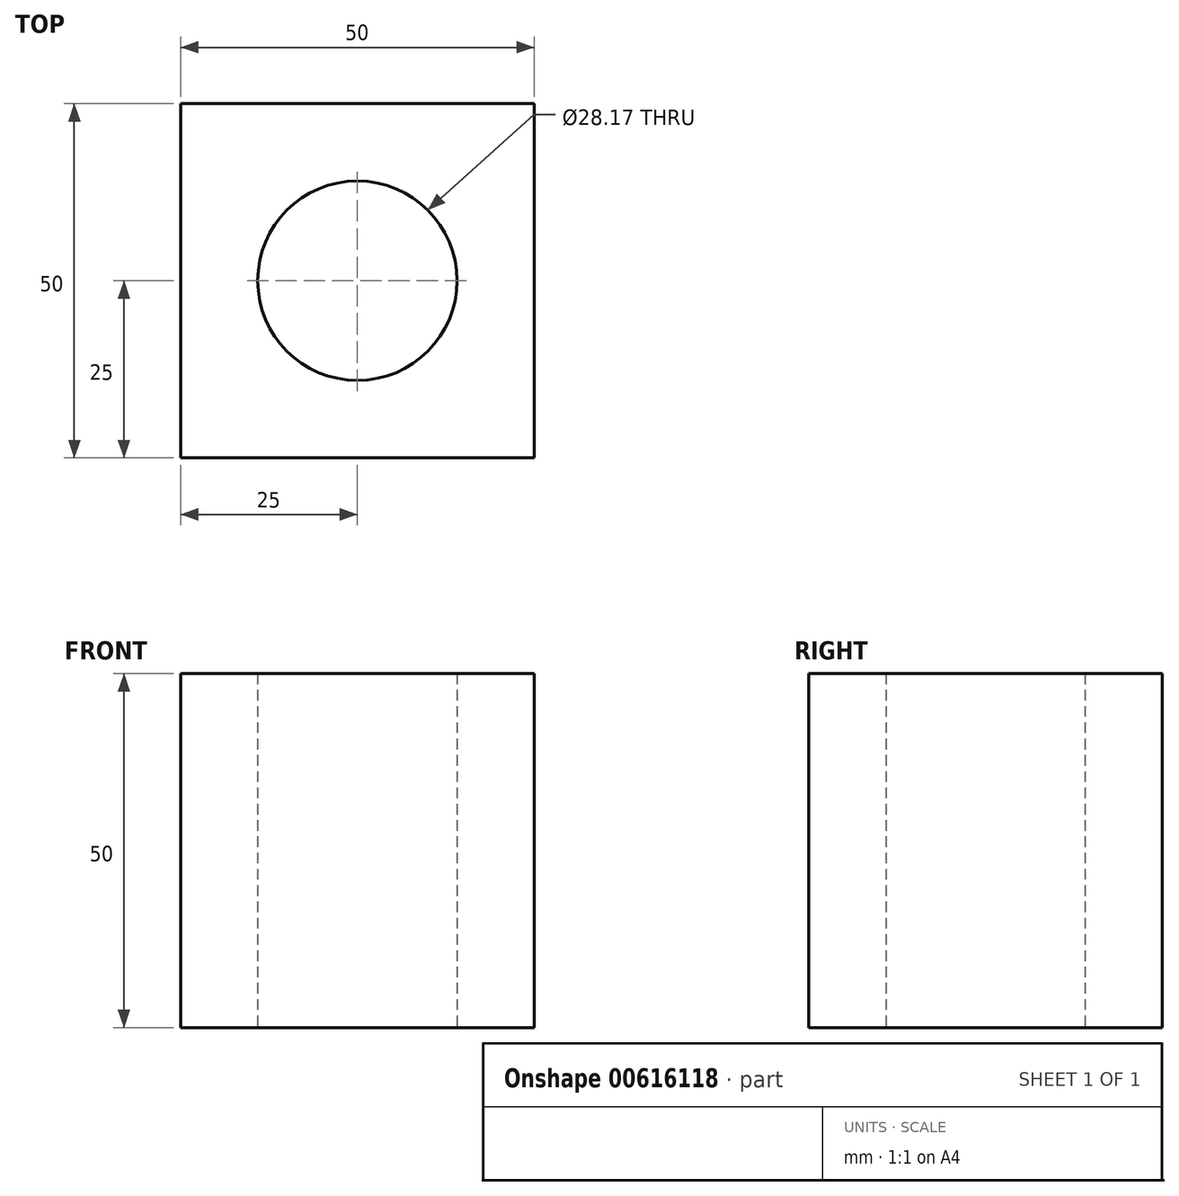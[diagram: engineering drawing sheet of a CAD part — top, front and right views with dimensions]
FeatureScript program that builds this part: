
annotation { "Feature Type Name" : "Feature", "Feature Type Description" : "" }
export const myFeature = defineFeature(function(context is Context, id is Id, definition is map)
    precondition{}
    {
        {
            var Q0;
            Q0=qCreatedBy(makeId("Top.planeOp"),FACE);
            var sketch = newSketch(context, id + "F0", { "sketchPlane" : qUnion([Q0])});
            skLineSegment(sketch, "E0.bottom", {"start": v(25, 25) * mm, "end": v(-25, 25) * mm});
            skLineSegment(sketch, "E0.top", {"start": v(25, -25) * mm, "end": v(-25, -25) * mm});
            skLineSegment(sketch, "E0.left", {"start": v(25, 25) * mm, "end": v(25, -25) * mm});
            skLineSegment(sketch, "E0.right", {"start": v(-25, 25) * mm, "end": v(-25, -25) * mm});
            skPoint(sketch, "E0.middle", {"position": v(0, 0) * mm});
            skSolve(sketch);
        }
        {
            var Q0;
            Q0=makeQuery(id+"F0.imprint","IMPRINT",FACE,{"disambiguationData":[TD([[makeQuery(id+"F0.imprint","IMPRINT",EDGE,{"derivedFrom":sQuery(id+"F0.wireOp",EDGE,"E0.bottom")}),1.0]])]});
            extrude(context, id + "F1", {"entities" : qUnion([Q0]), "depth" : 50 * mm, "offsetDistance" : 25 * mm});
        }
        {
            var Q0;
            Q0=qCreatedBy(makeId("Top.planeOp"),FACE);
            var sketch = newSketch(context, id + "F2", { "sketchPlane" : qUnion([Q0])});
            skCircle(sketch, "E1", {"center": v(0, 0) * mm, "radius": 14.09 * mm});
            skSolve(sketch);
        }
        {
            var Q0;
            Q0=makeQuery(id+"F2.imprint","IMPRINT",FACE,{"disambiguationData":[TD([[makeQuery(id+"F2.imprint","IMPRINT",EDGE,{"derivedFrom":sQuery(id+"F2.wireOp",EDGE,"E1")}),1.0]])]});
            extrude(context, id + "F3", {"entities" : qUnion([Q0]), "operationType" : NewBodyOperationType.REMOVE, "depth" : 50 * mm, "offsetDistance" : 25 * mm});
        }
    });
